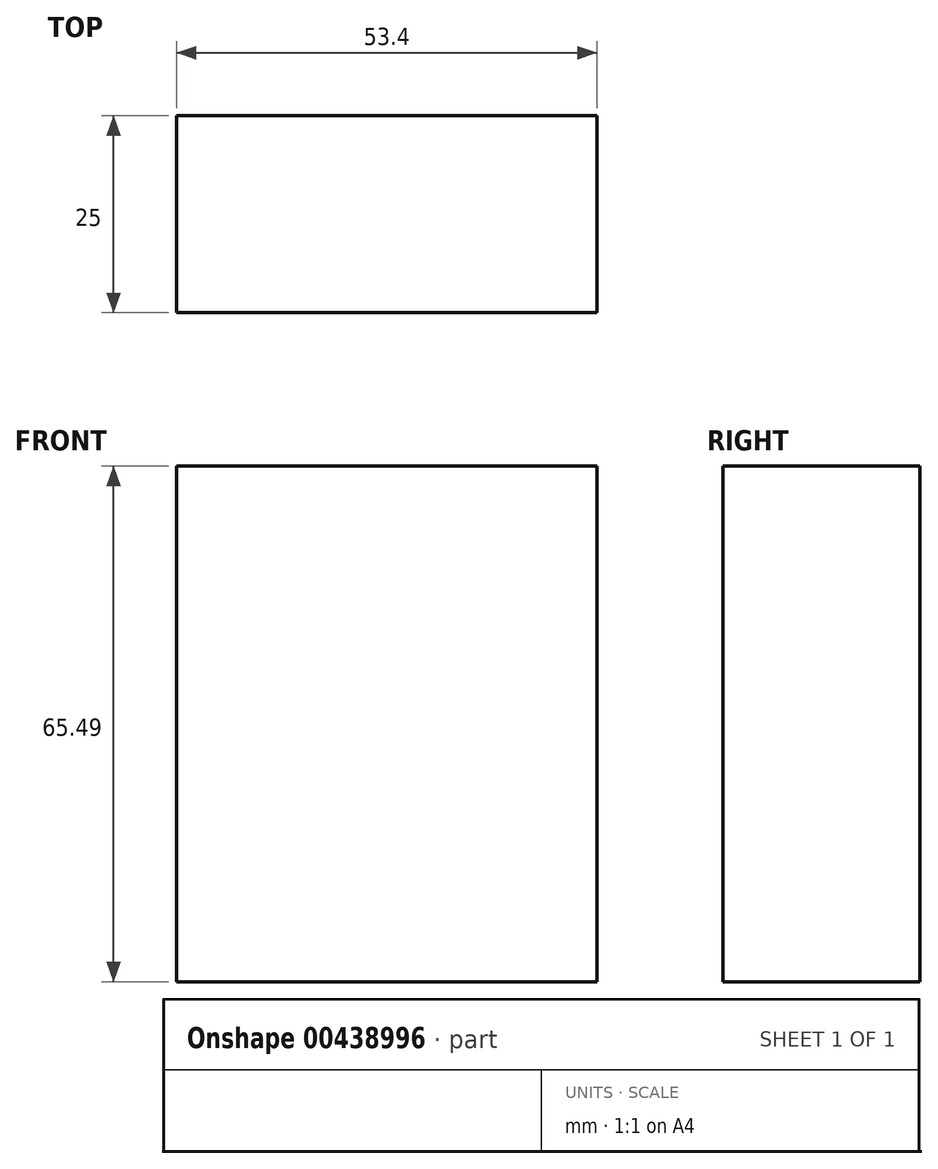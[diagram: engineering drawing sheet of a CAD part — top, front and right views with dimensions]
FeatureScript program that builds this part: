
annotation { "Feature Type Name" : "Feature", "Feature Type Description" : "" }
export const myFeature = defineFeature(function(context is Context, id is Id, definition is map)
    precondition{}
    {
        {
            var Q0;
            Q0=qCreatedBy(makeId("Front.planeOp"),FACE);
            var sketch = newSketch(context, id + "F0", { "sketchPlane" : qUnion([Q0])});
            skLineSegment(sketch, "E0.bottom", {"start": v(-104.14, -6.7) * mm, "end": v(-50.74, -6.7) * mm});
            skLineSegment(sketch, "E0.top", {"start": v(-104.14, 58.79) * mm, "end": v(-50.74, 58.79) * mm});
            skLineSegment(sketch, "E0.left", {"start": v(-104.14, -6.7) * mm, "end": v(-104.14, 58.79) * mm});
            skLineSegment(sketch, "E0.right", {"start": v(-50.74, -6.7) * mm, "end": v(-50.74, 58.79) * mm});
            skPoint(sketch, "E0.middle", {"position": v(-77.44, 26.04) * mm});
            skSolve(sketch);
        }
        {
            var Q0;
            Q0=makeQuery(id+"F0.imprint","IMPRINT",FACE,{"disambiguationData":[TD([[makeQuery(id+"F0.imprint","IMPRINT",EDGE,{"derivedFrom":sQuery(id+"F0.wireOp",EDGE,"E0.bottom")}),1.0]])]});
            extrude(context, id + "F1", {"entities" : qUnion([Q0]), "depth" : 25 * mm});
        }
    });
